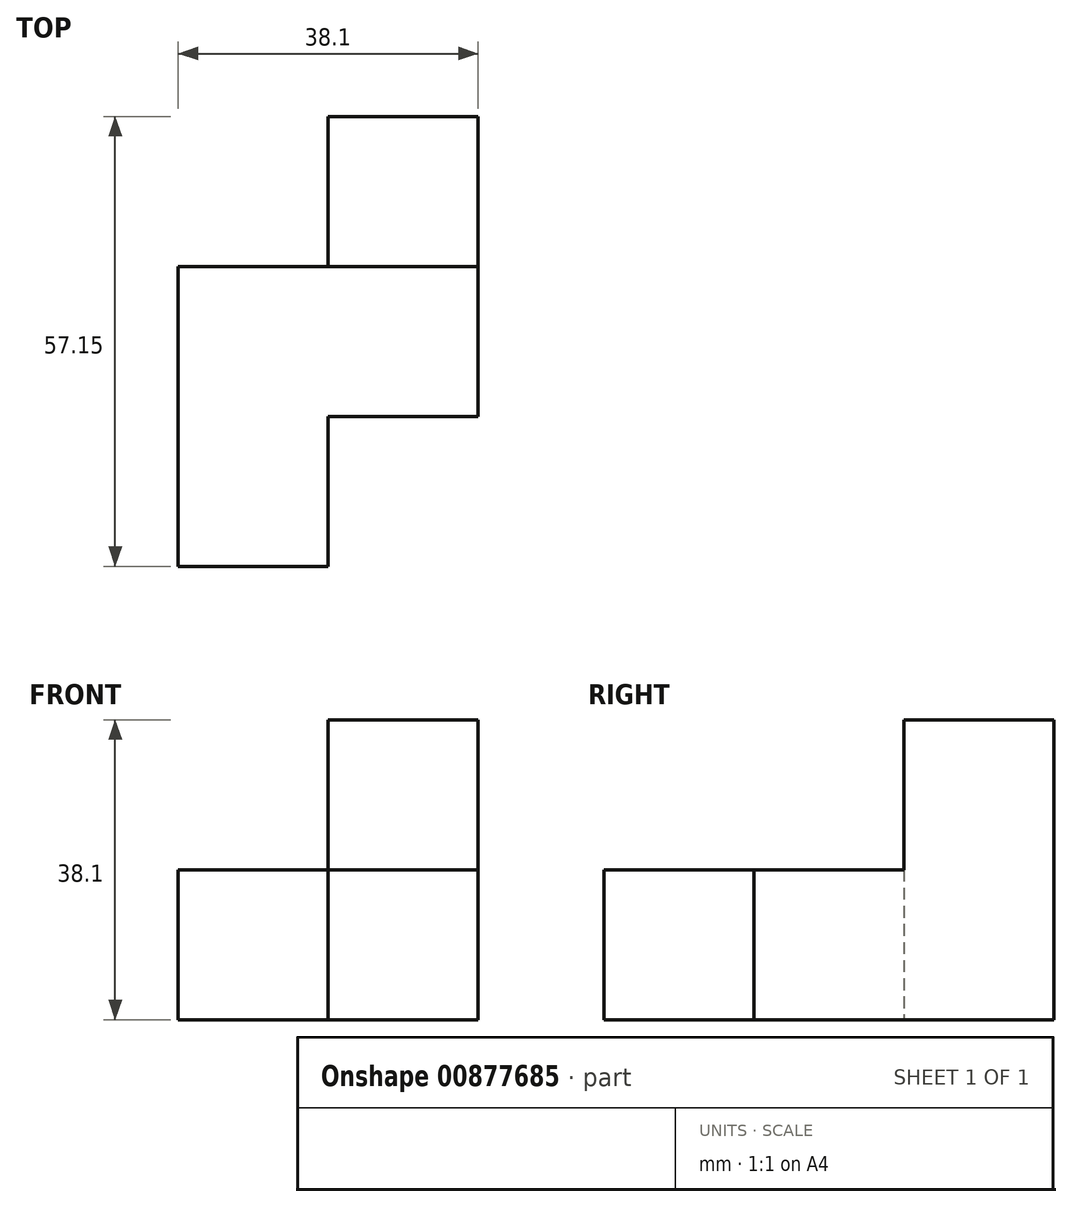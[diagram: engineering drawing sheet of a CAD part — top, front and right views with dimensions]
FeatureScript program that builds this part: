
annotation { "Feature Type Name" : "Feature", "Feature Type Description" : "" }
export const myFeature = defineFeature(function(context is Context, id is Id, definition is map)
    precondition{}
    {
        {
            var Q0;
            Q0=qCreatedBy(makeId("Top.planeOp"),FACE);
            var sketch = newSketch(context, id + "F0", { "sketchPlane" : qUnion([Q0])});
            skLineSegment(sketch, "E0", {"start": v(19.05, 0) * mm, "end": v(19.05, -19.05) * mm});
            skLineSegment(sketch, "E1", {"start": v(19.05, -19.05) * mm, "end": v(0, -19.05) * mm});
            skLineSegment(sketch, "E2", {"start": v(0, -19.05) * mm, "end": v(0, -57.15) * mm});
            skLineSegment(sketch, "E3", {"start": v(0, -57.15) * mm, "end": v(19.05, -57.15) * mm});
            skLineSegment(sketch, "E4", {"start": v(19.05, -57.15) * mm, "end": v(19.05, -38.1) * mm});
            skLineSegment(sketch, "E5", {"start": v(19.05, -38.1) * mm, "end": v(38.1, -38.1) * mm});
            skLineSegment(sketch, "E6", {"start": v(38.1, -38.1) * mm, "end": v(38.1, 0) * mm});
            skLineSegment(sketch, "E7", {"start": v(38.1, 0) * mm, "end": v(19.05, 0) * mm});
            skSolve(sketch);
        }
        {
            var Q0;
            Q0=qSketchRegion(id+"F0",true);
            extrude(context, id + "F1", {"entities" : qUnion([Q0]), "depth" : 19.05 * mm});
        }
        {
            var Q0;
            Q0=makeQuery(id+"F1.opExtrude","CAP_FACE",FACE,{"disambiguationData":[OSD([sQuery(id+"F0.wireOp",EDGE,"E0"),sQuery(id+"F0.wireOp",EDGE,"E1"),sQuery(id+"F0.wireOp",EDGE,"E2"),sQuery(id+"F0.wireOp",EDGE,"E3"),sQuery(id+"F0.wireOp",EDGE,"E4"),sQuery(id+"F0.wireOp",EDGE,"E5"),sQuery(id+"F0.wireOp",EDGE,"E6"),sQuery(id+"F0.wireOp",EDGE,"E7")])],"isStart":false});
            var sketch = newSketch(context, id + "F2", { "sketchPlane" : qUnion([Q0])});
            skLineSegment(sketch, "E8.bottom", {"start": v(19.05, 0) * mm, "end": v(38.1, 0) * mm});
            skLineSegment(sketch, "E8.top", {"start": v(19.05, -19.05) * mm, "end": v(38.1, -19.05) * mm});
            skLineSegment(sketch, "E8.left", {"start": v(19.05, 0) * mm, "end": v(19.05, -19.05) * mm});
            skLineSegment(sketch, "E8.right", {"start": v(38.1, 0) * mm, "end": v(38.1, -19.05) * mm});
            skSolve(sketch);
        }
        {
            var Q0;
            Q0=qSketchRegion(id+"F2",true);
            extrude(context, id + "F3", {"entities" : qUnion([Q0]), "operationType" : NewBodyOperationType.ADD, "depth" : 19.05 * mm});
        }
    });
